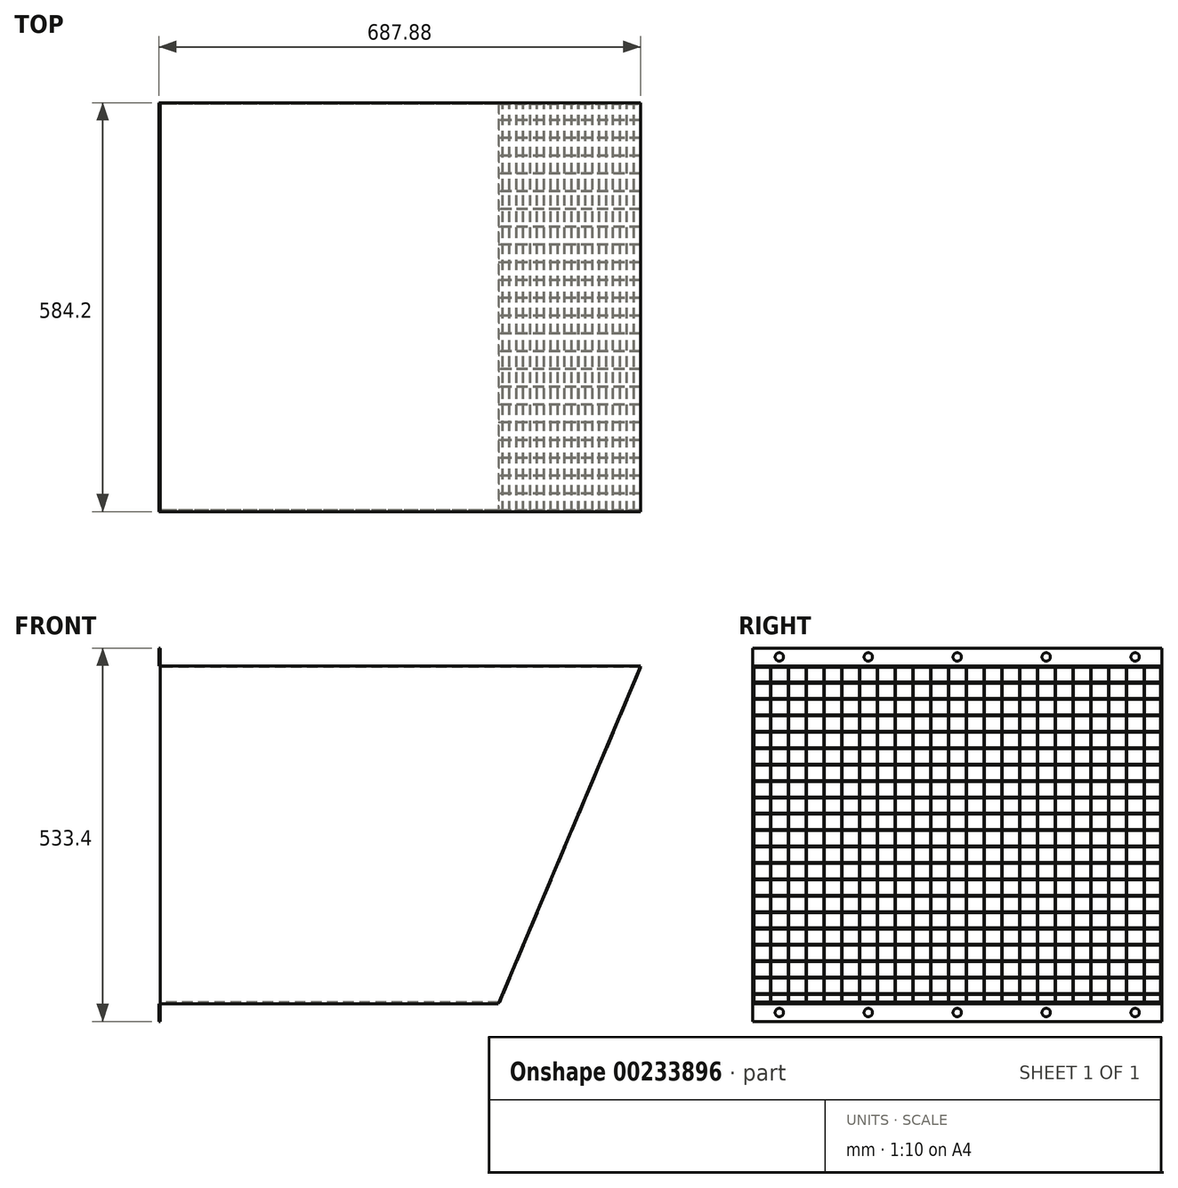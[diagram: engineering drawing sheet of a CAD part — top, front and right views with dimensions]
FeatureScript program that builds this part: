
annotation { "Feature Type Name" : "Feature", "Feature Type Description" : "" }
export const myFeature = defineFeature(function(context is Context, id is Id, definition is map)
    precondition{}
    {
        {
            var Q0;
            Q0=qCreatedBy(makeId("Right.planeOp"),FACE);
            var sketch = newSketch(context, id + "F0", { "sketchPlane" : qUnion([Q0])});
            skLineSegment(sketch, "E0.bottom", {"start": v(-292.1, 266.7) * mm, "end": v(292.1, 266.7) * mm});
            skLineSegment(sketch, "E0.top", {"start": v(-292.1, -266.7) * mm, "end": v(292.1, -266.7) * mm});
            skLineSegment(sketch, "E0.left", {"start": v(-292.1, 266.7) * mm, "end": v(-292.1, 241.3) * mm});
            skLineSegment(sketch, "E0.right", {"start": v(292.1, 266.7) * mm, "end": v(292.1, 241.3) * mm});
            skLineSegment(sketch, "E1", {"start": v(0, 266.7) * mm, "end": v(0, -266.7) * mm, "construction": true});
            skLineSegment(sketch, "E2", {"start": v(-292.1, 0) * mm, "end": v(292.1, 0) * mm, "construction": true});
            skLineSegment(sketch, "E3.0", {"start": v(-292.1, 241.3) * mm, "end": v(292.1, 241.3) * mm});
            skLineSegment(sketch, "E3.2", {"start": v(-292.1, -241.3) * mm, "end": v(292.1, -241.3) * mm});
            skLineSegment(sketch, "E4.trimOffspring", {"start": v(-292.1, -241.3) * mm, "end": v(-292.1, -266.7) * mm});
            skLineSegment(sketch, "E5.trimOffspring", {"start": v(292.1, -241.3) * mm, "end": v(292.1, -266.7) * mm});
            skSolve(sketch);
        }
        {
            var Q0;
            Q0 = qSketchRegion(id + "F0", true);
            extrude(context, id + "F1", {"entities" : qUnion([Q0]), "depth" : 2 * mm});
        }
        {
            var Q0;
            Q0=makeQuery(id+"F1.opExtrude","CAP_FACE",FACE,{"disambiguationData":[OSD([sQuery(id+"F0.wireOp",EDGE,"E0.bottom"),sQuery(id+"F0.wireOp",EDGE,"E0.top"),sQuery(id+"F0.wireOp",EDGE,"E0.left"),sQuery(id+"F0.wireOp",EDGE,"E0.right"),sQuery(id+"F0.wireOp",EDGE,"E3.0"),sQuery(id+"F0.wireOp",EDGE,"E3.1"),sQuery(id+"F0.wireOp",EDGE,"E3.2"),sQuery(id+"F0.wireOp",EDGE,"E3.3")])],"isStart":false});
            var sketch = newSketch(context, id + "F2", { "sketchPlane" : qUnion([Q0])});
            skLineSegment(sketch, "E6.bottom", {"start": v(-292.1, 241.3) * mm, "end": v(292.1, 241.3) * mm});
            skLineSegment(sketch, "E6.top", {"start": v(-292.1, -241.3) * mm, "end": v(292.1, -241.3) * mm});
            skLineSegment(sketch, "E6.left", {"start": v(-292.1, 241.3) * mm, "end": v(-292.1, -241.3) * mm});
            skLineSegment(sketch, "E6.right", {"start": v(292.1, 241.3) * mm, "end": v(292.1, -241.3) * mm});
            skLineSegment(sketch, "E7.0", {"start": v(-290.1, 239.3) * mm, "end": v(-290.1, -239.3) * mm});
            skLineSegment(sketch, "E7.1", {"start": v(-290.1, 239.3) * mm, "end": v(290.1, 239.3) * mm});
            skLineSegment(sketch, "E7.2", {"start": v(290.1, 239.3) * mm, "end": v(290.1, -239.3) * mm});
            skLineSegment(sketch, "E7.3", {"start": v(-290.1, -239.3) * mm, "end": v(290.1, -239.3) * mm});
            skSolve(sketch);
        }
        {
            var Q0;
            Q0 = qSketchRegion(id + "F2", true);
            extrude(context, id + "F3", {"entities" : qUnion([Q0]), "operationType" : NewBodyOperationType.ADD, "depth" : 685.8 * mm});
        }
        {
            var Q0;
            Q0=makeQuery(id+"F3.opExtrude","SWEPT_FACE",FACE,{"disambiguationData":[OSD([sQuery(id+"F2.wireOp",EDGE,"E6.left")])]});
            var sketch = newSketch(context, id + "F4", { "sketchPlane" : qUnion([Q0])});
            skLineSegment(sketch, "E8", {"start": v(687.8, 241.3) * mm, "end": v(484.6, -241.3) * mm});
            skLineSegment(sketch, "E9", {"start": v(687.8, 241.3) * mm, "end": v(687.8, -241.3) * mm});
            skLineSegment(sketch, "E10", {"start": v(687.8, -241.3) * mm, "end": v(484.6, -241.3) * mm});
            skSolve(sketch);
        }
        {
            var Q0;
            Q0 = qSketchRegion(id + "F4", true);
            extrude(context, id + "F5", {"entities" : qUnion([Q0]), "operationType" : NewBodyOperationType.REMOVE, "endBound" : BoundingType.THROUGH_ALL, "oppositeDirection" : true, "depth" : 25.4 * mm});
        }
        {
            var Q0;
            Q0=makeQuery(id+"F5.boolean.opBoolean","COPY",FACE,{"derivedFrom":makeQuery(id+"F5.opExtrude","SWEPT_FACE",FACE,{"disambiguationData":[OSD([sQuery(id+"F4.wireOp",EDGE,"E8")])]})});
            var sketch = newSketch(context, id + "F6", { "sketchPlane" : qUnion([Q0])});
            skLineSegment(sketch, "E11", {"start": v(-266.7, 487.13) * mm, "end": v(-266.7, -32.17) * mm});
            skLineSegment(sketch, "E12.0", {"start": v(-265.7, 487.13) * mm, "end": v(-265.7, -32.17) * mm});
            skLineSegment(sketch, "E13", {"start": v(-265.7, 487.13) * mm, "end": v(-266.7, 487.13) * mm});
            skLineSegment(sketch, "E14", {"start": v(-266.7, -32.17) * mm, "end": v(-265.7, -32.17) * mm});
            skLineSegment(sketch, "E15.1.0.0", {"start": v(-241.3, 487.13) * mm, "end": v(-241.3, -32.17) * mm});
            skLineSegment(sketch, "E15.1.0.1", {"start": v(-240.3, 487.13) * mm, "end": v(-240.3, -32.17) * mm});
            skLineSegment(sketch, "E15.1.0.2", {"start": v(-240.3, 487.13) * mm, "end": v(-241.3, 487.13) * mm});
            skLineSegment(sketch, "E15.1.0.3", {"start": v(-241.3, -32.17) * mm, "end": v(-240.3, -32.17) * mm});
            skLineSegment(sketch, "E15.2.0.0", {"start": v(-215.9, 487.13) * mm, "end": v(-215.9, -32.17) * mm});
            skLineSegment(sketch, "E15.2.0.1", {"start": v(-214.9, 487.13) * mm, "end": v(-214.9, -32.17) * mm});
            skLineSegment(sketch, "E15.2.0.2", {"start": v(-214.9, 487.13) * mm, "end": v(-215.9, 487.13) * mm});
            skLineSegment(sketch, "E15.2.0.3", {"start": v(-215.9, -32.17) * mm, "end": v(-214.9, -32.17) * mm});
            skLineSegment(sketch, "E15.direction1", {"start": v(-266.7, -32.17) * mm, "end": v(-241.3, -32.17) * mm, "construction": true});
            skLineSegment(sketch, "E16.0.3.0", {"start": v(-190.5, 487.13) * mm, "end": v(-190.5, -32.17) * mm});
            skLineSegment(sketch, "E16.3.3.0", {"start": v(-189.5, 487.13) * mm, "end": v(-189.5, -32.17) * mm});
            skLineSegment(sketch, "E16.6.3.0", {"start": v(-189.5, 487.13) * mm, "end": v(-190.5, 487.13) * mm});
            skLineSegment(sketch, "E16.9.3.0", {"start": v(-190.5, -32.17) * mm, "end": v(-189.5, -32.17) * mm});
            skLineSegment(sketch, "E16.0.4.0", {"start": v(-165.1, 487.13) * mm, "end": v(-165.1, -32.17) * mm});
            skLineSegment(sketch, "E16.3.4.0", {"start": v(-164.1, 487.13) * mm, "end": v(-164.1, -32.17) * mm});
            skLineSegment(sketch, "E16.6.4.0", {"start": v(-164.1, 487.13) * mm, "end": v(-165.1, 487.13) * mm});
            skLineSegment(sketch, "E16.9.4.0", {"start": v(-165.1, -32.17) * mm, "end": v(-164.1, -32.17) * mm});
            skLineSegment(sketch, "E16.0.5.0", {"start": v(-139.7, 487.13) * mm, "end": v(-139.7, -32.17) * mm});
            skLineSegment(sketch, "E16.3.5.0", {"start": v(-138.7, 487.13) * mm, "end": v(-138.7, -32.17) * mm});
            skLineSegment(sketch, "E16.6.5.0", {"start": v(-138.7, 487.13) * mm, "end": v(-139.7, 487.13) * mm});
            skLineSegment(sketch, "E16.9.5.0", {"start": v(-139.7, -32.17) * mm, "end": v(-138.7, -32.17) * mm});
            skLineSegment(sketch, "E17.0.6.0", {"start": v(-114.3, 487.13) * mm, "end": v(-114.3, -32.17) * mm});
            skLineSegment(sketch, "E17.3.6.0", {"start": v(-113.3, 487.13) * mm, "end": v(-113.3, -32.17) * mm});
            skLineSegment(sketch, "E17.6.6.0", {"start": v(-113.3, 487.13) * mm, "end": v(-114.3, 487.13) * mm});
            skLineSegment(sketch, "E17.9.6.0", {"start": v(-114.3, -32.17) * mm, "end": v(-113.3, -32.17) * mm});
            skLineSegment(sketch, "E17.0.7.0", {"start": v(-88.9, 487.13) * mm, "end": v(-88.9, -32.17) * mm});
            skLineSegment(sketch, "E17.3.7.0", {"start": v(-87.9, 487.13) * mm, "end": v(-87.9, -32.17) * mm});
            skLineSegment(sketch, "E17.6.7.0", {"start": v(-87.9, 487.13) * mm, "end": v(-88.9, 487.13) * mm});
            skLineSegment(sketch, "E17.9.7.0", {"start": v(-88.9, -32.17) * mm, "end": v(-87.9, -32.17) * mm});
            skLineSegment(sketch, "E17.0.8.0", {"start": v(-63.5, 487.13) * mm, "end": v(-63.5, -32.17) * mm});
            skLineSegment(sketch, "E17.3.8.0", {"start": v(-62.5, 487.13) * mm, "end": v(-62.5, -32.17) * mm});
            skLineSegment(sketch, "E17.6.8.0", {"start": v(-62.5, 487.13) * mm, "end": v(-63.5, 487.13) * mm});
            skLineSegment(sketch, "E17.9.8.0", {"start": v(-63.5, -32.17) * mm, "end": v(-62.5, -32.17) * mm});
            skLineSegment(sketch, "E17.0.9.0", {"start": v(-38.1, 487.13) * mm, "end": v(-38.1, -32.17) * mm});
            skLineSegment(sketch, "E17.3.9.0", {"start": v(-37.1, 487.13) * mm, "end": v(-37.1, -32.17) * mm});
            skLineSegment(sketch, "E17.6.9.0", {"start": v(-37.1, 487.13) * mm, "end": v(-38.1, 487.13) * mm});
            skLineSegment(sketch, "E17.9.9.0", {"start": v(-38.1, -32.17) * mm, "end": v(-37.1, -32.17) * mm});
            skLineSegment(sketch, "E17.0.10.0", {"start": v(-12.7, 487.13) * mm, "end": v(-12.7, -32.17) * mm});
            skLineSegment(sketch, "E17.3.10.0", {"start": v(-11.7, 487.13) * mm, "end": v(-11.7, -32.17) * mm});
            skLineSegment(sketch, "E17.6.10.0", {"start": v(-11.7, 487.13) * mm, "end": v(-12.7, 487.13) * mm});
            skLineSegment(sketch, "E17.9.10.0", {"start": v(-12.7, -32.17) * mm, "end": v(-11.7, -32.17) * mm});
            skLineSegment(sketch, "E17.0.11.0", {"start": v(12.7, 487.13) * mm, "end": v(12.7, -32.17) * mm});
            skLineSegment(sketch, "E17.3.11.0", {"start": v(13.7, 487.13) * mm, "end": v(13.7, -32.17) * mm});
            skLineSegment(sketch, "E17.6.11.0", {"start": v(13.7, 487.13) * mm, "end": v(12.7, 487.13) * mm});
            skLineSegment(sketch, "E17.9.11.0", {"start": v(12.7, -32.17) * mm, "end": v(13.7, -32.17) * mm});
            skLineSegment(sketch, "E17.0.12.0", {"start": v(38.1, 487.13) * mm, "end": v(38.1, -32.17) * mm});
            skLineSegment(sketch, "E17.3.12.0", {"start": v(39.1, 487.13) * mm, "end": v(39.1, -32.17) * mm});
            skLineSegment(sketch, "E17.6.12.0", {"start": v(39.1, 487.13) * mm, "end": v(38.1, 487.13) * mm});
            skLineSegment(sketch, "E17.9.12.0", {"start": v(38.1, -32.17) * mm, "end": v(39.1, -32.17) * mm});
            skLineSegment(sketch, "E17.0.13.0", {"start": v(63.5, 487.13) * mm, "end": v(63.5, -32.17) * mm});
            skLineSegment(sketch, "E17.3.13.0", {"start": v(64.5, 487.13) * mm, "end": v(64.5, -32.17) * mm});
            skLineSegment(sketch, "E17.6.13.0", {"start": v(64.5, 487.13) * mm, "end": v(63.5, 487.13) * mm});
            skLineSegment(sketch, "E17.9.13.0", {"start": v(63.5, -32.17) * mm, "end": v(64.5, -32.17) * mm});
            skLineSegment(sketch, "E17.0.14.0", {"start": v(88.9, 487.13) * mm, "end": v(88.9, -32.17) * mm});
            skLineSegment(sketch, "E17.3.14.0", {"start": v(89.9, 487.13) * mm, "end": v(89.9, -32.17) * mm});
            skLineSegment(sketch, "E17.6.14.0", {"start": v(89.9, 487.13) * mm, "end": v(88.9, 487.13) * mm});
            skLineSegment(sketch, "E17.9.14.0", {"start": v(88.9, -32.17) * mm, "end": v(89.9, -32.17) * mm});
            skLineSegment(sketch, "E18.0.15.0", {"start": v(114.3, 487.13) * mm, "end": v(114.3, -32.17) * mm});
            skLineSegment(sketch, "E18.3.15.0", {"start": v(115.3, 487.13) * mm, "end": v(115.3, -32.17) * mm});
            skLineSegment(sketch, "E18.6.15.0", {"start": v(115.3, 487.13) * mm, "end": v(114.3, 487.13) * mm});
            skLineSegment(sketch, "E18.9.15.0", {"start": v(114.3, -32.17) * mm, "end": v(115.3, -32.17) * mm});
            skLineSegment(sketch, "E18.0.16.0", {"start": v(139.7, 487.13) * mm, "end": v(139.7, -32.17) * mm});
            skLineSegment(sketch, "E18.3.16.0", {"start": v(140.7, 487.13) * mm, "end": v(140.7, -32.17) * mm});
            skLineSegment(sketch, "E18.6.16.0", {"start": v(140.7, 487.13) * mm, "end": v(139.7, 487.13) * mm});
            skLineSegment(sketch, "E18.9.16.0", {"start": v(139.7, -32.17) * mm, "end": v(140.7, -32.17) * mm});
            skLineSegment(sketch, "E18.0.17.0", {"start": v(165.1, 487.13) * mm, "end": v(165.1, -32.17) * mm});
            skLineSegment(sketch, "E18.3.17.0", {"start": v(166.1, 487.13) * mm, "end": v(166.1, -32.17) * mm});
            skLineSegment(sketch, "E18.6.17.0", {"start": v(166.1, 487.13) * mm, "end": v(165.1, 487.13) * mm});
            skLineSegment(sketch, "E18.9.17.0", {"start": v(165.1, -32.17) * mm, "end": v(166.1, -32.17) * mm});
            skLineSegment(sketch, "E18.0.18.0", {"start": v(190.5, 487.13) * mm, "end": v(190.5, -32.17) * mm});
            skLineSegment(sketch, "E18.3.18.0", {"start": v(191.5, 487.13) * mm, "end": v(191.5, -32.17) * mm});
            skLineSegment(sketch, "E18.6.18.0", {"start": v(191.5, 487.13) * mm, "end": v(190.5, 487.13) * mm});
            skLineSegment(sketch, "E18.9.18.0", {"start": v(190.5, -32.17) * mm, "end": v(191.5, -32.17) * mm});
            skLineSegment(sketch, "E18.0.19.0", {"start": v(215.9, 487.13) * mm, "end": v(215.9, -32.17) * mm});
            skLineSegment(sketch, "E18.3.19.0", {"start": v(216.9, 487.13) * mm, "end": v(216.9, -32.17) * mm});
            skLineSegment(sketch, "E18.6.19.0", {"start": v(216.9, 487.13) * mm, "end": v(215.9, 487.13) * mm});
            skLineSegment(sketch, "E18.9.19.0", {"start": v(215.9, -32.17) * mm, "end": v(216.9, -32.17) * mm});
            skLineSegment(sketch, "E19.0.20.0", {"start": v(241.3, 487.13) * mm, "end": v(241.3, -32.17) * mm});
            skLineSegment(sketch, "E19.3.20.0", {"start": v(242.3, 487.13) * mm, "end": v(242.3, -32.17) * mm});
            skLineSegment(sketch, "E19.6.20.0", {"start": v(242.3, 487.13) * mm, "end": v(241.3, 487.13) * mm});
            skLineSegment(sketch, "E19.9.20.0", {"start": v(241.3, -32.17) * mm, "end": v(242.3, -32.17) * mm});
            skLineSegment(sketch, "E19.0.21.0", {"start": v(266.7, 487.13) * mm, "end": v(266.7, -32.17) * mm});
            skLineSegment(sketch, "E19.3.21.0", {"start": v(267.7, 487.13) * mm, "end": v(267.7, -32.17) * mm});
            skLineSegment(sketch, "E19.6.21.0", {"start": v(267.7, 487.13) * mm, "end": v(266.7, 487.13) * mm});
            skLineSegment(sketch, "E19.9.21.0", {"start": v(266.7, -32.17) * mm, "end": v(267.7, -32.17) * mm});
            skSolve(sketch);
        }
        {
            var Q0;
            Q0 = qSketchRegion(id + "F6", true);
            extrude(context, id + "F7", {"entities" : qUnion([Q0]), "depth" : 1 * mm});
        }
        {
            var Q0;
            {var subQ12=sQuery(id+"F6.wireOp",EDGE,"E13");Q0=makeQuery(id+"F6.imprint","IMPRINT",FACE,{"disambiguationData":[TD([[makeQuery(id+"F6.imprint","IMPRINT",EDGE,{"derivedFrom":subQ12}),-1.0]])]});}
            var sketch = newSketch(context, id + "F8", { "sketchPlane" : qUnion([Q0])});
            skLineSegment(sketch, "E20.bottom", {"start": v(-292.1, 463.9) * mm, "end": v(292.1, 463.9) * mm});
            skLineSegment(sketch, "E20.top", {"start": v(-292.1, 462.9) * mm, "end": v(292.1, 462.9) * mm});
            skLineSegment(sketch, "E20.left", {"start": v(-292.1, 463.9) * mm, "end": v(-292.1, 462.9) * mm});
            skLineSegment(sketch, "E20.right", {"start": v(292.1, 463.9) * mm, "end": v(292.1, 462.9) * mm});
            skLineSegment(sketch, "E21.0.1.0", {"start": v(-292.1, 438.5) * mm, "end": v(-292.1, 437.5) * mm});
            skLineSegment(sketch, "E21.0.1.1", {"start": v(-292.1, 438.5) * mm, "end": v(292.1, 438.5) * mm});
            skLineSegment(sketch, "E21.0.1.2", {"start": v(-292.1, 437.5) * mm, "end": v(292.1, 437.5) * mm});
            skLineSegment(sketch, "E21.0.1.3", {"start": v(292.1, 438.5) * mm, "end": v(292.1, 437.5) * mm});
            skLineSegment(sketch, "E21.0.2.0", {"start": v(-292.1, 413.1) * mm, "end": v(-292.1, 412.1) * mm});
            skLineSegment(sketch, "E21.0.2.1", {"start": v(-292.1, 413.1) * mm, "end": v(292.1, 413.1) * mm});
            skLineSegment(sketch, "E21.0.2.2", {"start": v(-292.1, 412.1) * mm, "end": v(292.1, 412.1) * mm});
            skLineSegment(sketch, "E21.0.2.3", {"start": v(292.1, 413.1) * mm, "end": v(292.1, 412.1) * mm});
            skLineSegment(sketch, "E21.0.3.0", {"start": v(-292.1, 387.7) * mm, "end": v(-292.1, 386.7) * mm});
            skLineSegment(sketch, "E21.0.3.1", {"start": v(-292.1, 387.7) * mm, "end": v(292.1, 387.7) * mm});
            skLineSegment(sketch, "E21.0.3.2", {"start": v(-292.1, 386.7) * mm, "end": v(292.1, 386.7) * mm});
            skLineSegment(sketch, "E21.0.3.3", {"start": v(292.1, 387.7) * mm, "end": v(292.1, 386.7) * mm});
            skLineSegment(sketch, "E21.0.4.0", {"start": v(-292.1, 362.3) * mm, "end": v(-292.1, 361.3) * mm});
            skLineSegment(sketch, "E21.0.4.1", {"start": v(-292.1, 362.3) * mm, "end": v(292.1, 362.3) * mm});
            skLineSegment(sketch, "E21.0.4.2", {"start": v(-292.1, 361.3) * mm, "end": v(292.1, 361.3) * mm});
            skLineSegment(sketch, "E21.0.4.3", {"start": v(292.1, 362.3) * mm, "end": v(292.1, 361.3) * mm});
            skLineSegment(sketch, "E21.0.5.0", {"start": v(-292.1, 336.9) * mm, "end": v(-292.1, 335.9) * mm});
            skLineSegment(sketch, "E21.0.5.1", {"start": v(-292.1, 336.9) * mm, "end": v(292.1, 336.9) * mm});
            skLineSegment(sketch, "E21.0.5.2", {"start": v(-292.1, 335.9) * mm, "end": v(292.1, 335.9) * mm});
            skLineSegment(sketch, "E21.0.5.3", {"start": v(292.1, 336.9) * mm, "end": v(292.1, 335.9) * mm});
            skLineSegment(sketch, "E21.0.6.0", {"start": v(-292.1, 311.5) * mm, "end": v(-292.1, 310.5) * mm});
            skLineSegment(sketch, "E21.0.6.1", {"start": v(-292.1, 311.5) * mm, "end": v(292.1, 311.5) * mm});
            skLineSegment(sketch, "E21.0.6.2", {"start": v(-292.1, 310.5) * mm, "end": v(292.1, 310.5) * mm});
            skLineSegment(sketch, "E21.0.6.3", {"start": v(292.1, 311.5) * mm, "end": v(292.1, 310.5) * mm});
            skLineSegment(sketch, "E21.0.7.0", {"start": v(-292.1, 286.1) * mm, "end": v(-292.1, 285.1) * mm});
            skLineSegment(sketch, "E21.0.7.1", {"start": v(-292.1, 286.1) * mm, "end": v(292.1, 286.1) * mm});
            skLineSegment(sketch, "E21.0.7.2", {"start": v(-292.1, 285.1) * mm, "end": v(292.1, 285.1) * mm});
            skLineSegment(sketch, "E21.0.7.3", {"start": v(292.1, 286.1) * mm, "end": v(292.1, 285.1) * mm});
            skLineSegment(sketch, "E21.0.8.0", {"start": v(-292.1, 260.7) * mm, "end": v(-292.1, 259.7) * mm});
            skLineSegment(sketch, "E21.0.8.1", {"start": v(-292.1, 260.7) * mm, "end": v(292.1, 260.7) * mm});
            skLineSegment(sketch, "E21.0.8.2", {"start": v(-292.1, 259.7) * mm, "end": v(292.1, 259.7) * mm});
            skLineSegment(sketch, "E21.0.8.3", {"start": v(292.1, 260.7) * mm, "end": v(292.1, 259.7) * mm});
            skLineSegment(sketch, "E21.0.9.0", {"start": v(-292.1, 235.3) * mm, "end": v(-292.1, 234.3) * mm});
            skLineSegment(sketch, "E21.0.9.1", {"start": v(-292.1, 235.3) * mm, "end": v(292.1, 235.3) * mm});
            skLineSegment(sketch, "E21.0.9.2", {"start": v(-292.1, 234.3) * mm, "end": v(292.1, 234.3) * mm});
            skLineSegment(sketch, "E21.0.9.3", {"start": v(292.1, 235.3) * mm, "end": v(292.1, 234.3) * mm});
            skLineSegment(sketch, "E21.0.10.0", {"start": v(-292.1, 209.9) * mm, "end": v(-292.1, 208.9) * mm});
            skLineSegment(sketch, "E21.0.10.1", {"start": v(-292.1, 209.9) * mm, "end": v(292.1, 209.9) * mm});
            skLineSegment(sketch, "E21.0.10.2", {"start": v(-292.1, 208.9) * mm, "end": v(292.1, 208.9) * mm});
            skLineSegment(sketch, "E21.0.10.3", {"start": v(292.1, 209.9) * mm, "end": v(292.1, 208.9) * mm});
            skLineSegment(sketch, "E21.0.11.0", {"start": v(-292.1, 184.5) * mm, "end": v(-292.1, 183.5) * mm});
            skLineSegment(sketch, "E21.0.11.1", {"start": v(-292.1, 184.5) * mm, "end": v(292.1, 184.5) * mm});
            skLineSegment(sketch, "E21.0.11.2", {"start": v(-292.1, 183.5) * mm, "end": v(292.1, 183.5) * mm});
            skLineSegment(sketch, "E21.0.11.3", {"start": v(292.1, 184.5) * mm, "end": v(292.1, 183.5) * mm});
            skLineSegment(sketch, "E21.0.12.0", {"start": v(-292.1, 159.1) * mm, "end": v(-292.1, 158.1) * mm});
            skLineSegment(sketch, "E21.0.12.1", {"start": v(-292.1, 159.1) * mm, "end": v(292.1, 159.1) * mm});
            skLineSegment(sketch, "E21.0.12.2", {"start": v(-292.1, 158.1) * mm, "end": v(292.1, 158.1) * mm});
            skLineSegment(sketch, "E21.0.12.3", {"start": v(292.1, 159.1) * mm, "end": v(292.1, 158.1) * mm});
            skLineSegment(sketch, "E21.0.13.0", {"start": v(-292.1, 133.7) * mm, "end": v(-292.1, 132.7) * mm});
            skLineSegment(sketch, "E21.0.13.1", {"start": v(-292.1, 133.7) * mm, "end": v(292.1, 133.7) * mm});
            skLineSegment(sketch, "E21.0.13.2", {"start": v(-292.1, 132.7) * mm, "end": v(292.1, 132.7) * mm});
            skLineSegment(sketch, "E21.0.13.3", {"start": v(292.1, 133.7) * mm, "end": v(292.1, 132.7) * mm});
            skLineSegment(sketch, "E21.0.14.0", {"start": v(-292.1, 108.3) * mm, "end": v(-292.1, 107.3) * mm});
            skLineSegment(sketch, "E21.0.14.1", {"start": v(-292.1, 108.3) * mm, "end": v(292.1, 108.3) * mm});
            skLineSegment(sketch, "E21.0.14.2", {"start": v(-292.1, 107.3) * mm, "end": v(292.1, 107.3) * mm});
            skLineSegment(sketch, "E21.0.14.3", {"start": v(292.1, 108.3) * mm, "end": v(292.1, 107.3) * mm});
            skLineSegment(sketch, "E21.0.15.0", {"start": v(-292.1, 82.9) * mm, "end": v(-292.1, 81.9) * mm});
            skLineSegment(sketch, "E21.0.15.1", {"start": v(-292.1, 82.9) * mm, "end": v(292.1, 82.9) * mm});
            skLineSegment(sketch, "E21.0.15.2", {"start": v(-292.1, 81.9) * mm, "end": v(292.1, 81.9) * mm});
            skLineSegment(sketch, "E21.0.15.3", {"start": v(292.1, 82.9) * mm, "end": v(292.1, 81.9) * mm});
            skLineSegment(sketch, "E21.0.16.0", {"start": v(-292.1, 57.5) * mm, "end": v(-292.1, 56.5) * mm});
            skLineSegment(sketch, "E21.0.16.1", {"start": v(-292.1, 57.5) * mm, "end": v(292.1, 57.5) * mm});
            skLineSegment(sketch, "E21.0.16.2", {"start": v(-292.1, 56.5) * mm, "end": v(292.1, 56.5) * mm});
            skLineSegment(sketch, "E21.0.16.3", {"start": v(292.1, 57.5) * mm, "end": v(292.1, 56.5) * mm});
            skLineSegment(sketch, "E21.0.17.0", {"start": v(-292.1, 32.1) * mm, "end": v(-292.1, 31.1) * mm});
            skLineSegment(sketch, "E21.0.17.1", {"start": v(-292.1, 32.1) * mm, "end": v(292.1, 32.1) * mm});
            skLineSegment(sketch, "E21.0.17.2", {"start": v(-292.1, 31.1) * mm, "end": v(292.1, 31.1) * mm});
            skLineSegment(sketch, "E21.0.17.3", {"start": v(292.1, 32.1) * mm, "end": v(292.1, 31.1) * mm});
            skLineSegment(sketch, "E21.0.18.0", {"start": v(-292.1, 6.7) * mm, "end": v(-292.1, 5.7) * mm});
            skLineSegment(sketch, "E21.0.18.1", {"start": v(-292.1, 6.7) * mm, "end": v(292.1, 6.7) * mm});
            skLineSegment(sketch, "E21.0.18.2", {"start": v(-292.1, 5.7) * mm, "end": v(292.1, 5.7) * mm});
            skLineSegment(sketch, "E21.0.18.3", {"start": v(292.1, 6.7) * mm, "end": v(292.1, 5.7) * mm});
            skLineSegment(sketch, "E21.0.19.0", {"start": v(-292.1, -18.7) * mm, "end": v(-292.1, -19.7) * mm});
            skLineSegment(sketch, "E21.0.19.1", {"start": v(-292.1, -18.7) * mm, "end": v(292.1, -18.7) * mm});
            skLineSegment(sketch, "E21.0.19.2", {"start": v(-292.1, -19.7) * mm, "end": v(292.1, -19.7) * mm});
            skLineSegment(sketch, "E21.0.19.3", {"start": v(292.1, -18.7) * mm, "end": v(292.1, -19.7) * mm});
            skLineSegment(sketch, "E21.direction1", {"start": v(-292.1, 462.9) * mm, "end": v(-266.7, 462.9) * mm, "construction": true});
            skLineSegment(sketch, "E21.direction2", {"start": v(-292.1, 462.9) * mm, "end": v(-292.1, 437.5) * mm, "construction": true});
            skSolve(sketch);
        }
        {
            var Q0;
            Q0 = qSketchRegion(id + "F8", true);
            extrude(context, id + "F9", {"entities" : qUnion([Q0]), "depth" : 1 * mm});
        }
        {
            var Q0;
            Q0=makeQuery(id+"F1.opExtrude","CAP_FACE",FACE,{"disambiguationData":[OSD([sQuery(id+"F0.wireOp",EDGE,"E0.bottom"),sQuery(id+"F0.wireOp",EDGE,"E0.left"),sQuery(id+"F0.wireOp",EDGE,"E0.right"),sQuery(id+"F0.wireOp",EDGE,"E3.0")])],"isStart":false});
            var sketch = newSketch(context, id + "F10", { "sketchPlane" : qUnion([Q0])});
            skPoint(sketch, "E22", {"position": v(-254, 254) * mm});
            skPoint(sketch, "E23", {"position": v(-127, 254) * mm});
            skPoint(sketch, "E24", {"position": v(127, 254) * mm});
            skPoint(sketch, "E25", {"position": v(254, 254) * mm});
            skPoint(sketch, "E26", {"position": v(-254, -254) * mm});
            skPoint(sketch, "E27", {"position": v(-127, -254) * mm});
            skPoint(sketch, "E28", {"position": v(127, -254) * mm});
            skPoint(sketch, "E29", {"position": v(254, -254) * mm});
            skLineSegment(sketch, "E30", {"start": v(0, 0) * mm, "end": v(0, 266.7) * mm, "construction": true});
            skPoint(sketch, "E30.endSnap0", {"position": v(0, 266.7) * mm});
            skPoint(sketch, "E31", {"position": v(0, 254) * mm});
            skPoint(sketch, "E32", {"position": v(0, -254) * mm});
            skCircle(sketch, "E33", {"center": v(-254, 254) * mm, "radius": 6 * mm});
            skCircle(sketch, "E34", {"center": v(-127, 254) * mm, "radius": 6 * mm});
            skCircle(sketch, "E35", {"center": v(0, 254) * mm, "radius": 6 * mm});
            skCircle(sketch, "E36", {"center": v(127, 254) * mm, "radius": 6 * mm});
            skCircle(sketch, "E37", {"center": v(254, 254) * mm, "radius": 6 * mm});
            skCircle(sketch, "E38", {"center": v(-254, -254) * mm, "radius": 6 * mm});
            skCircle(sketch, "E39", {"center": v(-127, -254) * mm, "radius": 6 * mm});
            skCircle(sketch, "E40", {"center": v(0, -254) * mm, "radius": 6 * mm});
            skCircle(sketch, "E41", {"center": v(127, -254) * mm, "radius": 6 * mm});
            skCircle(sketch, "E42", {"center": v(254, -254) * mm, "radius": 6 * mm});
            skSolve(sketch);
        }
        {
            var Q0;
            Q0 = qSketchRegion(id + "F10", true);
            extrude(context, id + "F11", {"entities" : qUnion([Q0]), "operationType" : NewBodyOperationType.REMOVE, "oppositeDirection" : true, "depth" : 25.4 * mm});
        }
    });
